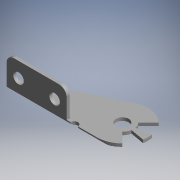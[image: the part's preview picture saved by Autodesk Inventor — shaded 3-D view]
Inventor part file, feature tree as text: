
AUTODESK INVENTOR PART (.ipt)
format: ipt  version: 2017.3 (Build 213256000, 256)  size: 167,424 bytes
history: native  units: mm (DEFAULTED — no unit token found)
features: other x28, sketch x6, extrude x4, hole x2
ambient origin geometry x8: Origin, YZ Plane, XZ Plane, XY Plane, X Axis, Y Axis, Z Axis, Center Point
bodies: Solid1 (feature_tree)
feature tree (40):
  extrude  "Extrusion1"  Depth=120.0mm TaperAngle=0.0deg
  extrude  "Extrusion2"  Depth=2.0mm TaperAngle=0.0deg
  extrude  "Extrusion3"  [1 undecoded]
  hole  "Hole1"  [1 undecoded]
  hole  "Hole2"  [1 undecoded]
  extrude  "Extrusion4"  [1 undecoded]
  other  "fix_end_l_XY"
  other  "fix_end_l_YZ"
  other  "fix_end_l_ZX"
  other  "fix_end_l_X"
  other  "fix_end_l_Y"
  other  "fix_end_l_Z"
  other  "fix_end_l_Center"
  other  "free_end_l_XY"
  other  "free_end_l_YZ"
  other  "free_end_l_ZX"
  other  "free_end_l_X"
  other  "free_end_l_Y"
  other  "free_end_l_Z"
  other  "free_end_l_Center"
  other  "l_to_r_XY"
  other  "l_to_r_YZ"
  other  "l_to_r_ZX"
  other  "l_to_r_X"
  other  "l_to_r_Y"
  other  "l_to_r_Z"
  other  "l_to_r_Center"
  other  "to_clip1_XY"
  other  "to_clip1_YZ"
  other  "to_clip1_ZX"
  other  "to_clip1_X"
  other  "to_clip1_Y"
  other  "to_clip1_Z"
  other  "to_clip1_Center"
  sketch  "Sketch_1"  dims[d0=20.0mm d1=0.0mm d2=120.0mm d3=0.0mm]
  sketch  "Sketch_2"  dims[d4=34.0mm d5=0.0mm]
  sketch  "Sketch_3"  dims[d6=7.0mm d7=6.0mm d8=4.0mm d9=2.0mm d10=90.0deg d11=2.0mm d12=0.0mm]
  sketch  "Sketch4"  dims[d13=7.0mm d14=6.0mm d15=4.0mm d16=2.0mm d17=90.0deg d18=2.0mm d19=0.0mm d20=20.0mm d21=0.0mm]
  sketch  "Sketch5"  dims[d22=0.0mm d23=0.0mm]
  sketch  "Sketch_7"
note: 4 required parameter values undecoded (feature->parameter linkage not recoverable at this tier; creation-order binding heuristic only, values carry confidence <= 0.55)
